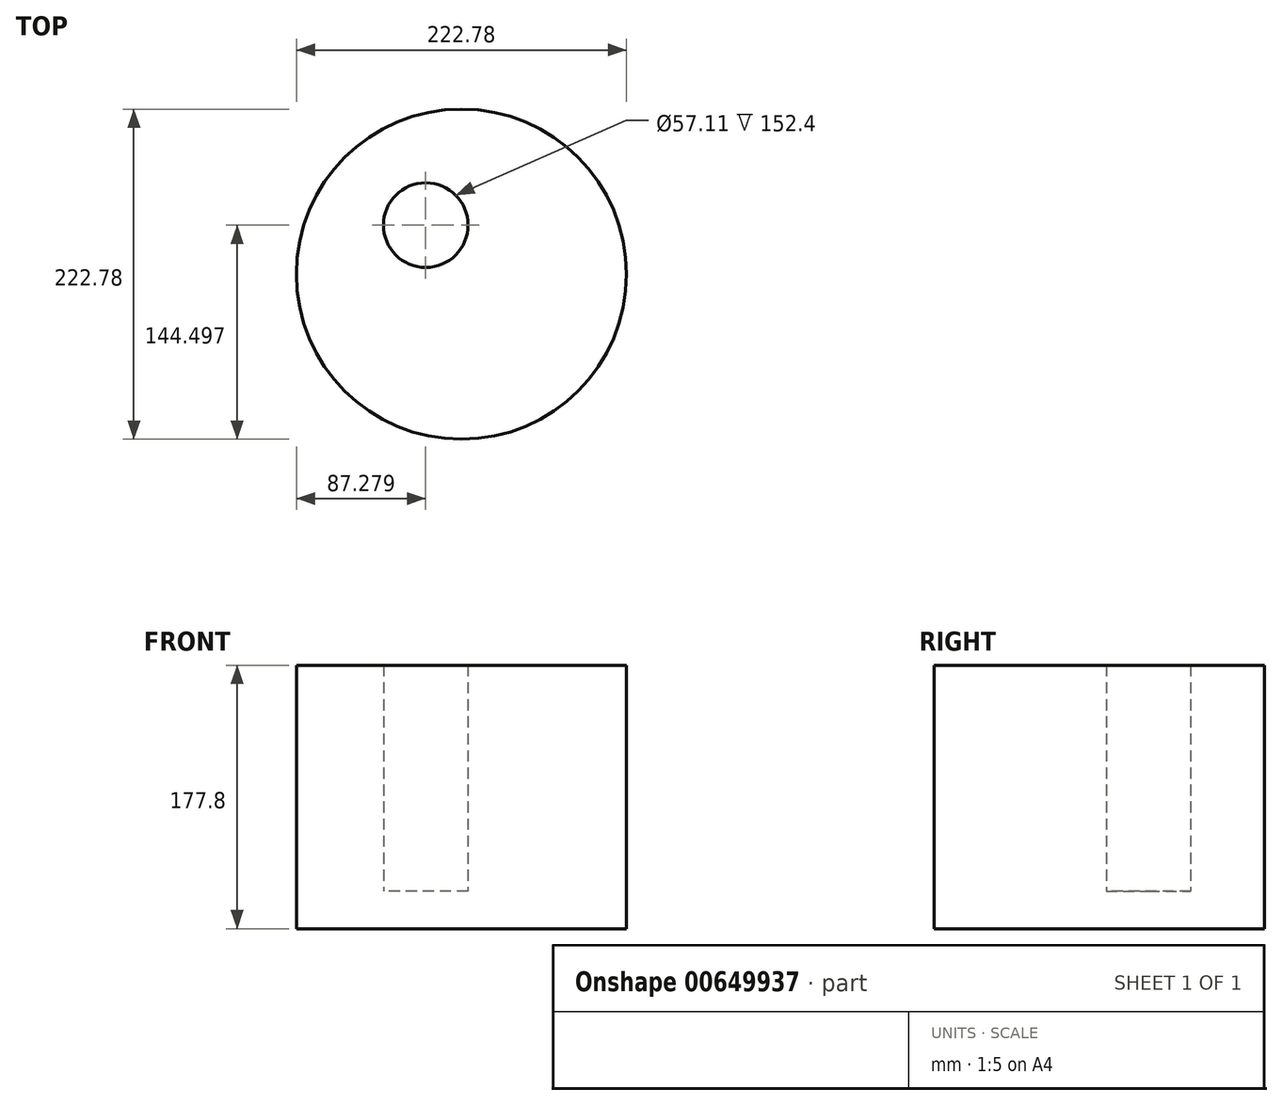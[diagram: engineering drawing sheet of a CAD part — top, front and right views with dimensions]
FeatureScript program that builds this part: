
annotation { "Feature Type Name" : "Feature", "Feature Type Description" : "" }
export const myFeature = defineFeature(function(context is Context, id is Id, definition is map)
    precondition{}
    {
        {
            var Q0;
            Q0=qCreatedBy(makeId("Top.planeOp"),FACE);
            var sketch = newSketch(context, id + "F0", { "sketchPlane" : qUnion([Q0])});
            skCircle(sketch, "E0", {"center": v(0, 0) * mm, "radius": 111.4 * mm});
            skSolve(sketch);
        }
        {
            var Q0;
            Q0 = qSketchRegion(id + "F0", true);
            var sketch = newSketch(context, id + "F1", { "sketchPlane" : qUnion([Q0])});
            skSolve(sketch);
        }
        {
            var Q0;
            Q0=makeQuery(id+"F1.imprint","IMPRINT",FACE,{"disambiguationData":[TD([[makeQuery(id+"F1.imprint","IMPRINT",EDGE,{"derivedFrom":makeQuery(id+"F0.imprint","IMPRINT",EDGE,{"derivedFrom":sQuery(id+"F0.wireOp",EDGE,"E0")})}),1.0]])]});
            extrude(context, id + "F2", {"entities" : qUnion([Q0]), "depth" : 25.4 * mm, "offsetDistance" : 25.4 * mm});
        }
        {
            var Q0;
            Q0=makeQuery(id+"F2.opExtrude","CAP_FACE",FACE,{"disambiguationData":[OSD([sQuery(id+"F0.wireOp",EDGE,"E0")])],"isStart":false});
            var sketch = newSketch(context, id + "F3", { "sketchPlane" : qUnion([Q0])});
            skCircle(sketch, "E1", {"center": v(-24.11, 33.1) * mm, "radius": 28.56 * mm});
            skSolve(sketch);
        }
        {
            var Q0;
            Q0=makeQuery(id+"F3.imprint","IMPRINT",FACE,{"disambiguationData":[TD([[makeQuery(id+"F3.imprint","IMPRINT",EDGE,{"derivedFrom":sQuery(id+"F3.wireOp",EDGE,"E1")}),-1.0]])]});
            extrude(context, id + "F4", {"entities" : qUnion([Q0]), "operationType" : NewBodyOperationType.ADD, "depth" : 25.4 * mm, "offsetDistance" : 25.4 * mm});
        }
        {
            var Q0;
            Q0=makeQuery(id+"F4.opExtrude","CAP_FACE",FACE,{"disambiguationData":[OSD([sQuery(id+"F0.wireOp",EDGE,"E0"),sQuery(id+"F3.wireOp",EDGE,"E1")])],"isStart":false});
            var sketch = newSketch(context, id + "F5", { "sketchPlane" : qUnion([Q0])});
            skLineSegment(sketch, "E2.bottom", {"start": v(0, -42.43) * mm, "end": v(62.3, -42.43) * mm});
            skLineSegment(sketch, "E2.top", {"start": v(0, -92.34) * mm, "end": v(62.3, -92.34) * mm});
            skLineSegment(sketch, "E2.left", {"start": v(0, -42.43) * mm, "end": v(0, -92.34) * mm});
            skLineSegment(sketch, "E2.right", {"start": v(62.3, -42.43) * mm, "end": v(62.3, -92.34) * mm});
            skSolve(sketch);
        }
        {
            var Q0;
            Q0 = qSketchRegion(id + "F5", true);
            var Q1;
            Q1=makeQuery(id+"F5.imprint","IMPRINT",FACE,{"disambiguationData":[TD([[makeQuery(id+"F5.imprint","IMPRINT",EDGE,{"derivedFrom":sQuery(id+"F5.wireOp",EDGE,"E2.bottom")}),1.0]])]});
            extrude(context, id + "F6", {"entities" : qUnion([Q0, Q1]), "operationType" : NewBodyOperationType.ADD, "depth" : 127 * mm, "offsetDistance" : 25.4 * mm});
        }
    });
